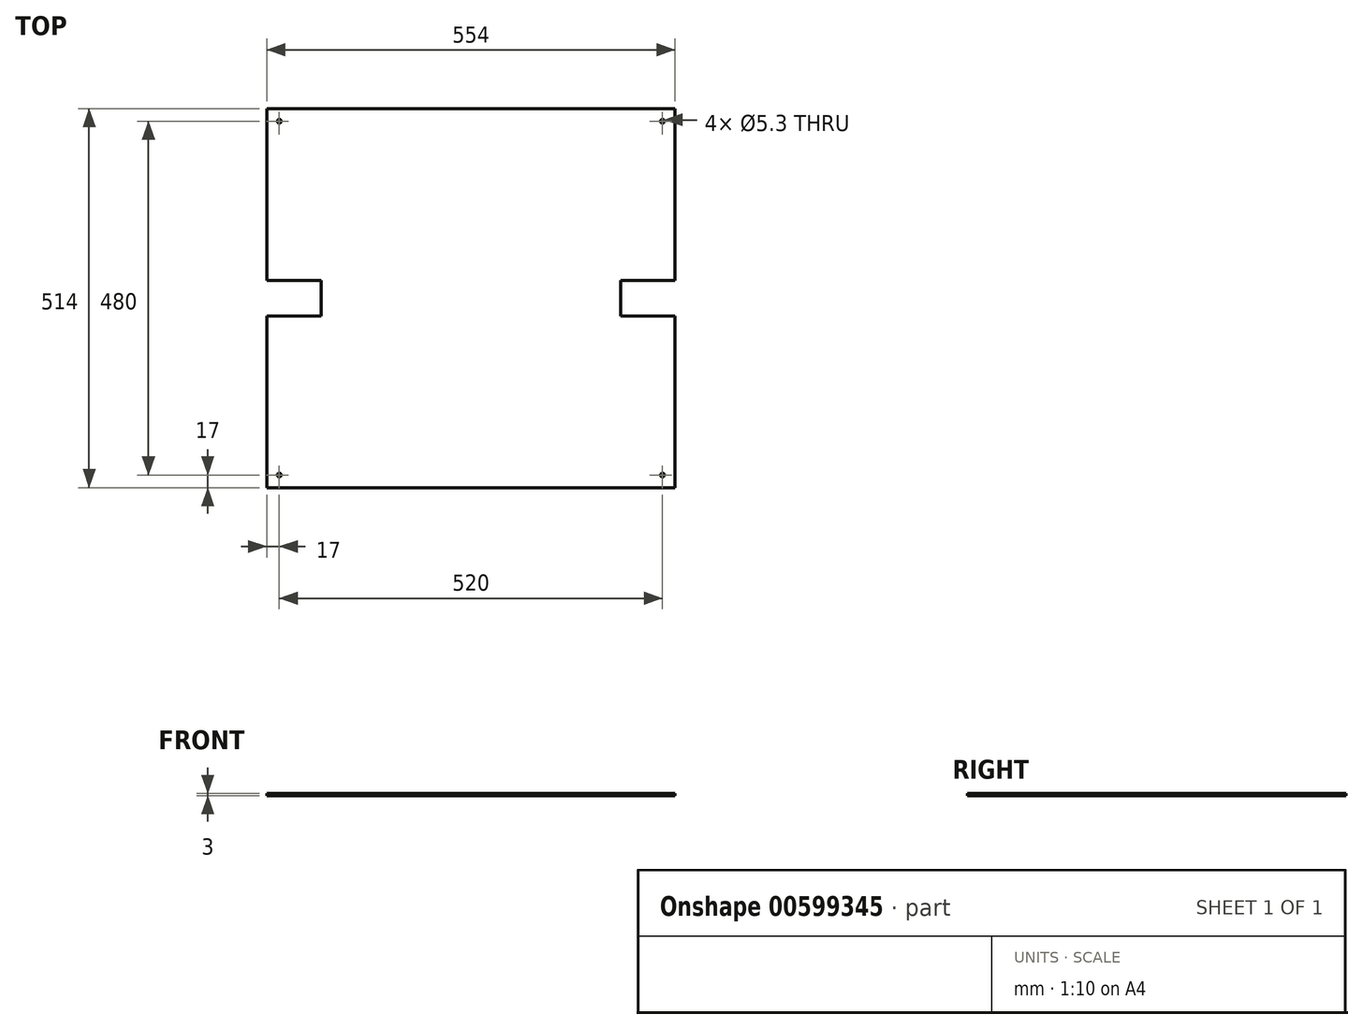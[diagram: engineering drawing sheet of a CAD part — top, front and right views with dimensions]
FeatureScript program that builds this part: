
annotation { "Feature Type Name" : "Feature", "Feature Type Description" : "" }
export const myFeature = defineFeature(function(context is Context, id is Id, definition is map)
    precondition{}
    {
        {
            var Q0;
            Q0=qCreatedBy(makeId("Top.planeOp"),FACE);
            var sketch = newSketch(context, id + "F0", { "sketchPlane" : qUnion([Q0])});
            skLineSegment(sketch, "E0.bottom", {"start": v(-270, 250) * mm, "end": v(270, 250) * mm, "construction": true});
            skLineSegment(sketch, "E0.top", {"start": v(-270, -250) * mm, "end": v(270, -250) * mm, "construction": true});
            skLineSegment(sketch, "E0.left", {"start": v(-270, 250) * mm, "end": v(-270, -250) * mm, "construction": true});
            skLineSegment(sketch, "E0.right", {"start": v(270, 250) * mm, "end": v(270, -250) * mm, "construction": true});
            skCircle(sketch, "E1", {"center": v(-260, -240) * mm, "radius": 2.65 * mm});
            skCircle(sketch, "E2", {"center": v(-260, 240) * mm, "radius": 2.65 * mm});
            skCircle(sketch, "E3", {"center": v(260, 240) * mm, "radius": 2.65 * mm});
            skCircle(sketch, "E4", {"center": v(260, -240) * mm, "radius": 2.65 * mm});
            skLineSegment(sketch, "E5.bottom", {"start": v(-277, -257) * mm, "end": v(277, -257) * mm});
            skLineSegment(sketch, "E5.top", {"start": v(-277, 257) * mm, "end": v(277, 257) * mm});
            skLineSegment(sketch, "E5.left", {"start": v(-277, -257) * mm, "end": v(-277, -24) * mm});
            skLineSegment(sketch, "E5.right", {"start": v(277, -257) * mm, "end": v(277, -24) * mm});
            skLineSegment(sketch, "E6.bottom", {"start": v(-277, -24) * mm, "end": v(-203, -24) * mm});
            skLineSegment(sketch, "E7.trimOffspring", {"start": v(-277, 24) * mm, "end": v(-277, 257) * mm});
            skLineSegment(sketch, "E8.MirrorCS", {"start": v(-277, 24) * mm, "end": v(-203, 24) * mm});
            skLineSegment(sketch, "E9.MirrorCS", {"start": v(277, 24) * mm, "end": v(203, 24) * mm});
            skLineSegment(sketch, "E10.MirrorCS", {"start": v(277, -24) * mm, "end": v(203, -24) * mm});
            skLineSegment(sketch, "E11.trimOffspring", {"start": v(277, 24) * mm, "end": v(277, 257) * mm});
            skPoint(sketch, "E12.orphan", {"position": v(0, 257) * mm});
            skLineSegment(sketch, "E13", {"start": v(-203, -24) * mm, "end": v(-203, 24) * mm});
            skLineSegment(sketch, "E14", {"start": v(203, 24) * mm, "end": v(203, -24) * mm});
            skSolve(sketch);
        }
        {
            var Q0;
            Q0=qSketchRegion(id+"F0",true);
            extrude(context, id + "F1", {"entities" : qUnion([Q0]), "depth" : 3 * mm});
        }
    });
